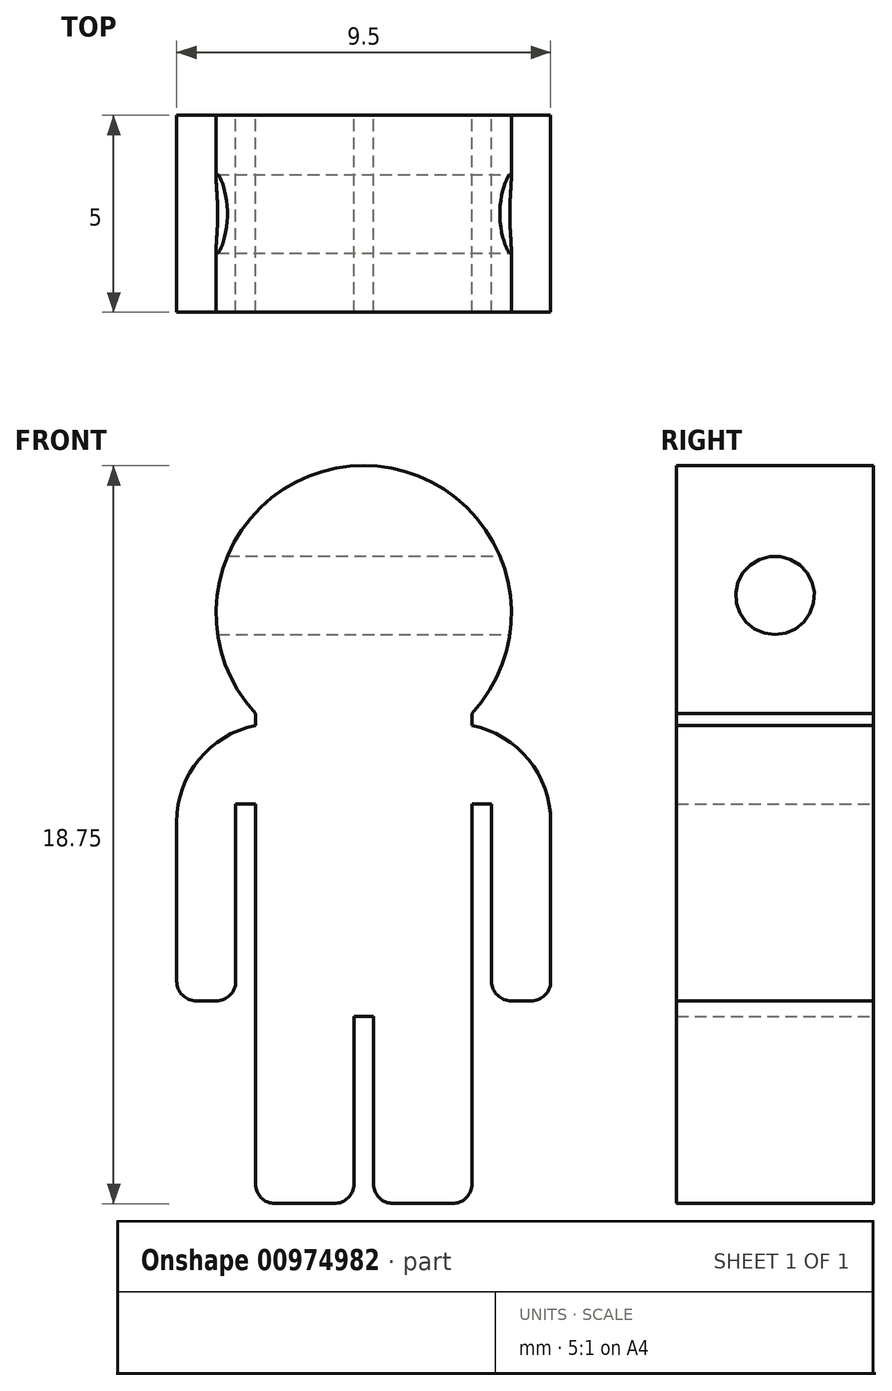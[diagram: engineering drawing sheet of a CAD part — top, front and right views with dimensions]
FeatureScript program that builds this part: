
annotation { "Feature Type Name" : "Feature", "Feature Type Description" : "" }
export const myFeature = defineFeature(function(context is Context, id is Id, definition is map)
    precondition{}
    {
        {
            var Q0;
            Q0=qCreatedBy(makeId("Front.planeOp"),FACE);
            var sketch = newSketch(context, id + "F0", { "sketchPlane" : qUnion([Q0])});
            skLineSegment(sketch, "E0.bottom", {"start": v(-11, 16.37) * mm, "end": v(0, 16.37) * mm});
            skLineSegment(sketch, "E0.top", {"start": v(-11, -13.63) * mm, "end": v(0, -13.63) * mm});
            skLineSegment(sketch, "E0.left", {"start": v(-11, 16.37) * mm, "end": v(-11, -13.63) * mm});
            skLineSegment(sketch, "E0.right", {"start": v(0, 16.37) * mm, "end": v(0, -13.63) * mm});
            skCircle(sketch, "E1", {"center": v(-5.5, 16.37) * mm, "radius": 7.5 * mm});
            skLineSegment(sketch, "E2.bottom", {"start": v(-11, 10.66) * mm, "end": v(-15, 10.66) * mm});
            skLineSegment(sketch, "E2.top", {"start": v(-11, -3.34) * mm, "end": v(-15, -3.34) * mm});
            skLineSegment(sketch, "E2.left", {"start": v(-11, 10.66) * mm, "end": v(-11, -3.34) * mm});
            skLineSegment(sketch, "E2.right", {"start": v(-15, 10.66) * mm, "end": v(-15, -3.34) * mm});
            skLineSegment(sketch, "E3.bottom", {"start": v(0, 10.66) * mm, "end": v(4, 10.66) * mm});
            skLineSegment(sketch, "E3.top", {"start": v(0, -3.34) * mm, "end": v(4, -3.34) * mm});
            skLineSegment(sketch, "E3.left", {"start": v(0, 10.66) * mm, "end": v(0, -3.34) * mm});
            skLineSegment(sketch, "E3.right", {"start": v(4, 10.66) * mm, "end": v(4, -3.34) * mm});
            skLineSegment(sketch, "E4.bottom", {"start": v(-6, -4.13) * mm, "end": v(-5, -4.13) * mm});
            skLineSegment(sketch, "E4.top", {"start": v(-6, -13.63) * mm, "end": v(-5, -13.63) * mm});
            skLineSegment(sketch, "E4.left", {"start": v(-6, -4.13) * mm, "end": v(-6, -13.63) * mm});
            skLineSegment(sketch, "E4.right", {"start": v(-5, -4.13) * mm, "end": v(-5, -13.63) * mm});
            skLineSegment(sketch, "E5.bottom", {"start": v(-12, 6.66) * mm, "end": v(-11, 6.66) * mm});
            skLineSegment(sketch, "E5.top", {"start": v(-12, -3.34) * mm, "end": v(-11, -3.34) * mm});
            skLineSegment(sketch, "E5.left", {"start": v(-12, 6.66) * mm, "end": v(-12, -3.34) * mm});
            skLineSegment(sketch, "E5.right", {"start": v(-11, 6.66) * mm, "end": v(-11, -3.34) * mm});
            skLineSegment(sketch, "E6.bottom", {"start": v(0, 6.66) * mm, "end": v(1, 6.66) * mm});
            skLineSegment(sketch, "E6.top", {"start": v(0, -3.34) * mm, "end": v(1, -3.34) * mm});
            skLineSegment(sketch, "E6.left", {"start": v(0, 6.66) * mm, "end": v(0, -3.34) * mm});
            skLineSegment(sketch, "E6.right", {"start": v(1, 6.66) * mm, "end": v(1, -3.34) * mm});
            skSolve(sketch);
        }
        {
            var Q0;
            {var subQ0=sQuery(id+"F0.wireOp",EDGE,"E0.bottom");Q0=makeQuery(id+"F0.imprint","IMPRINT",FACE,{"disambiguationData":[TD([[makeQuery(id+"F0.imprint","IMPRINT",EDGE,{"derivedFrom":subQ0}),1.0]])]});}
            var Q1;
            {var subQ0=sQuery(id+"F0.wireOp",EDGE,"E0.bottom");Q1=makeQuery(id+"F0.imprint","IMPRINT",FACE,{"disambiguationData":[TD([[makeQuery(id+"F0.imprint","IMPRINT",EDGE,{"derivedFrom":subQ0}),-1.0]])]});}
            var Q2;
            {var subQ0=sQuery(id+"F0.wireOp",EDGE,"E0.top");Q2=makeQuery(id+"F0.imprint","IMPRINT",FACE,{"disambiguationData":[TD([[makeQuery(id+"F0.imprint","IMPRINT",EDGE,{"derivedFrom":subQ0}),1.0]])]});}
            var Q3;
            Q3=makeQuery(id+"F0.imprint","IMPRINT",FACE,{"disambiguationData":[TD([[makeQuery(id+"F0.imprint","IMPRINT",EDGE,{"derivedFrom":sQuery(id+"F0.wireOp",EDGE,"E2.bottom")}),1.0]])]});
            var Q4;
            Q4=makeQuery(id+"F0.imprint","IMPRINT",FACE,{"disambiguationData":[TD([[makeQuery(id+"F0.imprint","IMPRINT",EDGE,{"derivedFrom":sQuery(id+"F0.wireOp",EDGE,"E3.bottom")}),-1.0]])]});
            extrude(context, id + "F1", {"entities" : qUnion([Q0, Q1, Q2, Q3, Q4]), "depth" : 10 * mm, "offsetDistance" : 25 * mm});
        }
        {
            var Q0;
            Q0=makeQuery(id+"F1.opExtrude","SWEPT_EDGE",EDGE,{"disambiguationData":[OSD([sQuery(id+"F0.wireOp",EDGE,"E3.bottom"),sQuery(id+"F0.wireOp",EDGE,"E3.right")])]});
            var Q1;
            Q1=makeQuery(id+"F1.opExtrude","SWEPT_EDGE",EDGE,{"disambiguationData":[OSD([sQuery(id+"F0.wireOp",EDGE,"E2.bottom"),sQuery(id+"F0.wireOp",EDGE,"E2.right")])]});
            fillet(context, id + "F2", {"entities" : qUnion([Q0, Q1]), "radius" : 5 * mm, "tangentPropagation" : true, "allowEdgeOverflow" : false});
        }
        {
            var Q0;
            Q0=makeQuery(id+"F1.opExtrude","SWEPT_EDGE",EDGE,{"disambiguationData":[OSD([sQuery(id+"F0.wireOp",EDGE,"E2.top"),sQuery(id+"F0.wireOp",EDGE,"E2.right")])]});
            var Q1;
            Q1=makeQuery(id+"F1.opExtrude","SWEPT_EDGE",EDGE,{"disambiguationData":[OSD([sQuery(id+"F0.wireOp",EDGE,"E2.top"),sQuery(id+"F0.wireOp",EDGE,"E5.top"),sQuery(id+"F0.wireOp",EDGE,"E5.left")])]});
            var Q2;
            Q2=makeQuery(id+"F1.opExtrude","SWEPT_EDGE",EDGE,{"disambiguationData":[OSD([sQuery(id+"F0.wireOp",EDGE,"E3.top"),sQuery(id+"F0.wireOp",EDGE,"E6.top"),sQuery(id+"F0.wireOp",EDGE,"E6.right")])]});
            var Q3;
            Q3=makeQuery(id+"F1.opExtrude","SWEPT_EDGE",EDGE,{"disambiguationData":[OSD([sQuery(id+"F0.wireOp",EDGE,"E3.top"),sQuery(id+"F0.wireOp",EDGE,"E3.right")])]});
            var Q4;
            Q4=makeQuery(id+"F1.opExtrude","SWEPT_EDGE",EDGE,{"disambiguationData":[OSD([sQuery(id+"F0.wireOp",EDGE,"E0.top"),sQuery(id+"F0.wireOp",EDGE,"E4.top"),sQuery(id+"F0.wireOp",EDGE,"E4.right")])]});
            var Q5;
            Q5=makeQuery(id+"F1.opExtrude","SWEPT_EDGE",EDGE,{"disambiguationData":[OSD([sQuery(id+"F0.wireOp",EDGE,"E0.top"),sQuery(id+"F0.wireOp",EDGE,"E0.right")])]});
            var Q6;
            Q6=makeQuery(id+"F1.opExtrude","SWEPT_EDGE",EDGE,{"disambiguationData":[OSD([sQuery(id+"F0.wireOp",EDGE,"E0.top"),sQuery(id+"F0.wireOp",EDGE,"E0.left")])]});
            var Q7;
            Q7=makeQuery(id+"F1.opExtrude","SWEPT_EDGE",EDGE,{"disambiguationData":[OSD([sQuery(id+"F0.wireOp",EDGE,"E0.top"),sQuery(id+"F0.wireOp",EDGE,"E4.top"),sQuery(id+"F0.wireOp",EDGE,"E4.left")])]});
            fillet(context, id + "F3", {"entities" : qUnion([Q0, Q1, Q2, Q3, Q4, Q5, Q6, Q7]), "radius" : 1 * mm, "tangentPropagation" : true, "allowEdgeOverflow" : false});
        }
        {
            var Q0;
            Q0=makeQuery(id+"F1.opExtrude","SWEPT_BODY",BODY,{"disambiguationData":[OSD([sQuery(id+"F0.wireOp",EDGE,"E0.top"),sQuery(id+"F0.wireOp",EDGE,"E0.left"),sQuery(id+"F0.wireOp",EDGE,"E0.right"),sQuery(id+"F0.wireOp",EDGE,"E1"),sQuery(id+"F0.wireOp",EDGE,"E2.bottom"),sQuery(id+"F0.wireOp",EDGE,"E2.top"),sQuery(id+"F0.wireOp",EDGE,"E2.right"),sQuery(id+"F0.wireOp",EDGE,"E3.bottom"),sQuery(id+"F0.wireOp",EDGE,"E3.top"),sQuery(id+"F0.wireOp",EDGE,"E3.right"),sQuery(id+"F0.wireOp",EDGE,"E4.bottom"),sQuery(id+"F0.wireOp",EDGE,"E4.left"),sQuery(id+"F0.wireOp",EDGE,"E4.right"),sQuery(id+"F0.wireOp",EDGE,"E5.bottom"),sQuery(id+"F0.wireOp",EDGE,"E5.left"),sQuery(id+"F0.wireOp",EDGE,"E5.right"),sQuery(id+"F0.wireOp",EDGE,"E6.bottom"),sQuery(id+"F0.wireOp",EDGE,"E6.left"),sQuery(id+"F0.wireOp",EDGE,"E6.right")])]});
            var Q1;
            Q1=qCreatedBy(makeId("Origin.pointOp"),VERTEX);
            transform(context, id + "F4", {"entities" : qUnion([Q0]), "transformType" : TransformType.SCALE_UNIFORMLY, "scale" : 0.5, "scalePoint" : qUnion([Q1]), "makeCopy" : false});
        }
        {
            var Q0;
            Q0=qCreatedBy(makeId("Right.planeOp"),FACE);
            var sketch = newSketch(context, id + "F5", { "sketchPlane" : qUnion([Q0])});
            skCircle(sketch, "E7", {"center": v(-2.5, 8.63) * mm, "radius": 1 * mm});
            skSolve(sketch);
        }
        {
            var Q0;
            Q0 = qSketchRegion(id + "F5", true);
            extrude(context, id + "F6", {"entities" : qUnion([Q0]), "operationType" : NewBodyOperationType.REMOVE, "oppositeDirection" : true, "depth" : 25 * mm, "offsetDistance" : 25 * mm, "hasSecondDirection" : true, "secondDirectionOppositeDirection" : false, "secondDirectionDepth" : 25 * mm});
        }
    });
